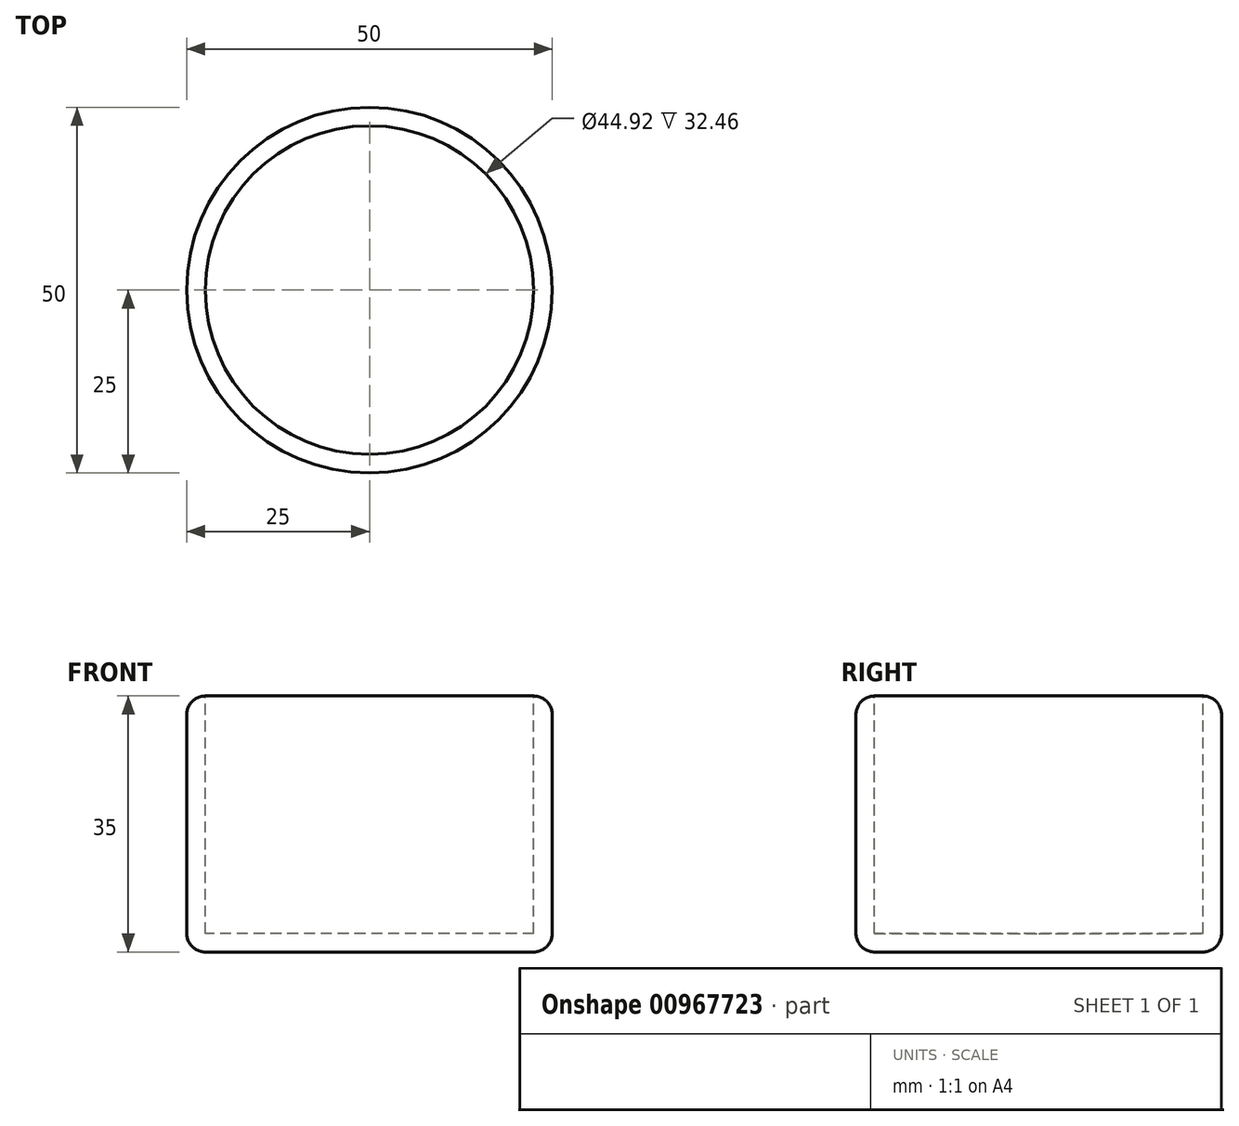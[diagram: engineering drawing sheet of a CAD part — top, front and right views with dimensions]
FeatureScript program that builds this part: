
annotation { "Feature Type Name" : "Feature", "Feature Type Description" : "" }
export const myFeature = defineFeature(function(context is Context, id is Id, definition is map)
    precondition{}
    {
        {
            var Q0;
            Q0=qCreatedBy(makeId("Front.planeOp"),FACE);
            var sketch = newSketch(context, id + "F0", { "sketchPlane" : qUnion([Q0])});
            skLineSegment(sketch, "E0", {"start": v(0, 1.6) * mm, "end": v(0, -33.4) * mm});
            skLineSegment(sketch, "E1", {"start": v(0, -33.4) * mm, "end": v(-25, -33.4) * mm});
            skLineSegment(sketch, "E2", {"start": v(-25, -33.4) * mm, "end": v(-25, 1.6) * mm});
            skLineSegment(sketch, "E3", {"start": v(-25, 1.6) * mm, "end": v(0, 1.6) * mm});
            skSolve(sketch);
        }
        {
            var Q0;
            Q0=makeQuery(id+"F0.imprint","IMPRINT",FACE,{"disambiguationData":[TD([[makeQuery(id+"F0.imprint","IMPRINT",EDGE,{"derivedFrom":sQuery(id+"F0.wireOp",EDGE,"E0")}),-1.0]])]});
            var Q1;
            Q1 = qSketchRegion(id + "F0", true);
            var Q2;
            Q2=sQuery(id+"F0.wireOp",EDGE,"E0");
            revolve(context, id + "F1", {"surfaceOperationType" : NewSurfaceOperationType.NEW, "entities" : qUnion([Q0, Q1]), "axis" : qUnion([Q2]), "revolveType" : RevolveType.FULL});
        }
        {
            var Q0;
            Q0=makeQuery(id+"F1.opRevolve","SWEPT_EDGE",EDGE,{"disambiguationData":[OSD([sQuery(id+"F0.wireOp",EDGE,"E2"),sQuery(id+"F0.wireOp",EDGE,"E3")])]});
            var Q1;
            Q1=makeQuery(id+"F1.opRevolve","SWEPT_EDGE",EDGE,{"disambiguationData":[OSD([sQuery(id+"F0.wireOp",EDGE,"E1"),sQuery(id+"F0.wireOp",EDGE,"E2")])]});
            fillet(context, id + "F2", {"entities" : qUnion([Q0, Q1]), "radius" : 2.54 * mm, "tangentPropagation" : true, "allowEdgeOverflow" : false});
        }
        {
            var Q0;
            Q0=makeQuery(id+"F1.opRevolve","SWEPT_FACE",FACE,{"disambiguationData":[OSD([sQuery(id+"F0.wireOp",EDGE,"E3")])]});
            shell(context, id + "F3", {"entities" : qUnion([Q0]), "thickness" : 2.54 * mm});
        }
    });
